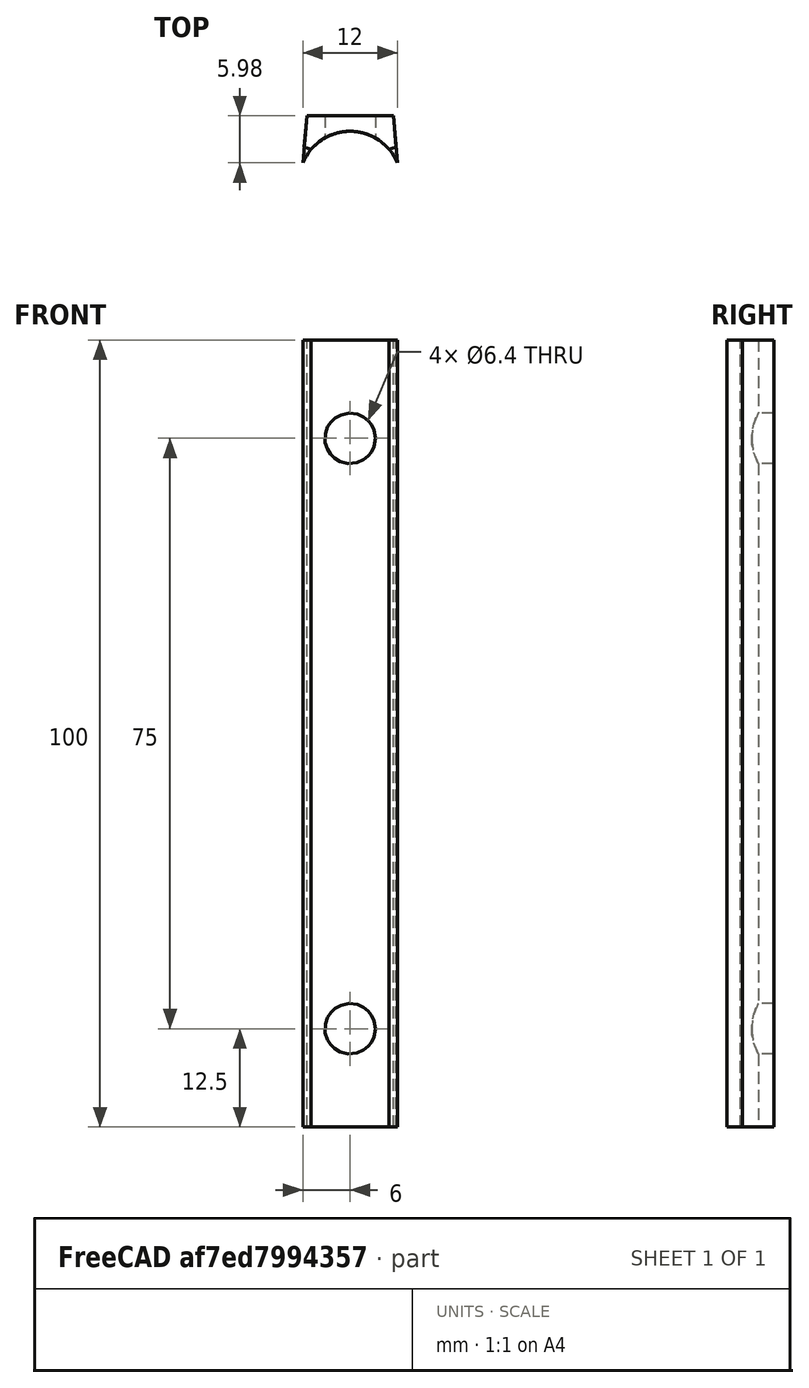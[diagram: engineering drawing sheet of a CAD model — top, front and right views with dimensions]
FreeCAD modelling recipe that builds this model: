
FCSTD DOCUMENT  (FreeCAD 0.16R)
Label: Cargispacertop
License: All rights reserved
LicenseURL: http://en.wikipedia.org/wiki/All_rights_reserved
objects: Part::Cut×3, Sketcher::SketchObject×2, Part::Cylinder×2, PartDesign::Pad×1, PartDesign::Chamfer×1, Mesh::Feature×1
note: 10 computed .brp shape members not serialized (recipe doc carries the construction recipe); baked Part::Feature solids carry a one-line shape summary decoded from their .brp

FEATURE [Sketcher::SketchObject] Sketch
FEATURE [Sketcher::SketchObject] Sketch001
  sketch-geometry (4):
    g0: ArcOfCircle CenterX=0 CenterY=-8.47913 CenterZ=0 NormalX=0 NormalY=0 NormalZ=1 Radius=6.5 StartAngle=0.394791 EndAngle=2.7468
    g1: LineSegment StartX=-5.5 StartY=0 StartZ=0 EndX=-6 EndY=-5.97913 EndZ=0
    g2: LineSegment StartX=5.5 StartY=0 StartZ=0 EndX=6 EndY=-5.97913 EndZ=0
    g3: LineSegment StartX=-5.5 StartY=0 StartZ=0 EndX=5.5 EndY=0 EndZ=0
  constraints (12):
    c: Radius(g0) = 6.5
    c: Coincident(g1,g0)
    c: Coincident(g2,g0)
    c: Equal(g1,g2)
    c: Symmetric(g0,g0,g-2)
    c: Distance(g2) = 6
    c: PointOnObject(g2,g-1)
    c: Coincident(g3,g1)
    c: Horizontal(g3)
    c: Coincident(g2,g3)
    c: Distance(g0,g0) = 12
    c: Distance(g2,g1) = 11
FEATURE [PartDesign::Pad] Pad
  Length = 100
  Length2 = 100
  Midplane = true
  Sketch = -> Sketch001
  Type = 0
FEATURE [Part::Cylinder] Cylinder
  Angle = 360
  Height = 10
  Placement = pos=(0,2,37.5) rot=(1,0,0;1.5708rad)
  Radius = 3.2
FEATURE [Part::Cut] Cut
  Base = -> Pad
  Tool = -> Cylinder
FEATURE [Part::Cylinder] Cylinder001
  Angle = 360
  Height = 10
  Placement = pos=(0,2,-37.5) rot=(1,0,0;1.5708rad)
  Radius = 3.2
FEATURE [Part::Cut] Cut001
  Base = -> Cut
  Tool = -> Cylinder001
FEATURE [Part::Cut] Cut002
  Base = -> Cut
  Tool = -> Cylinder001
FEATURE [PartDesign::Chamfer] Chamfer
  Base = -> Cut002 [Edge1,Edge4]
  Size = 2
FEATURE [Mesh::Feature] Mesh  label="Chamfer (Meshed)"
